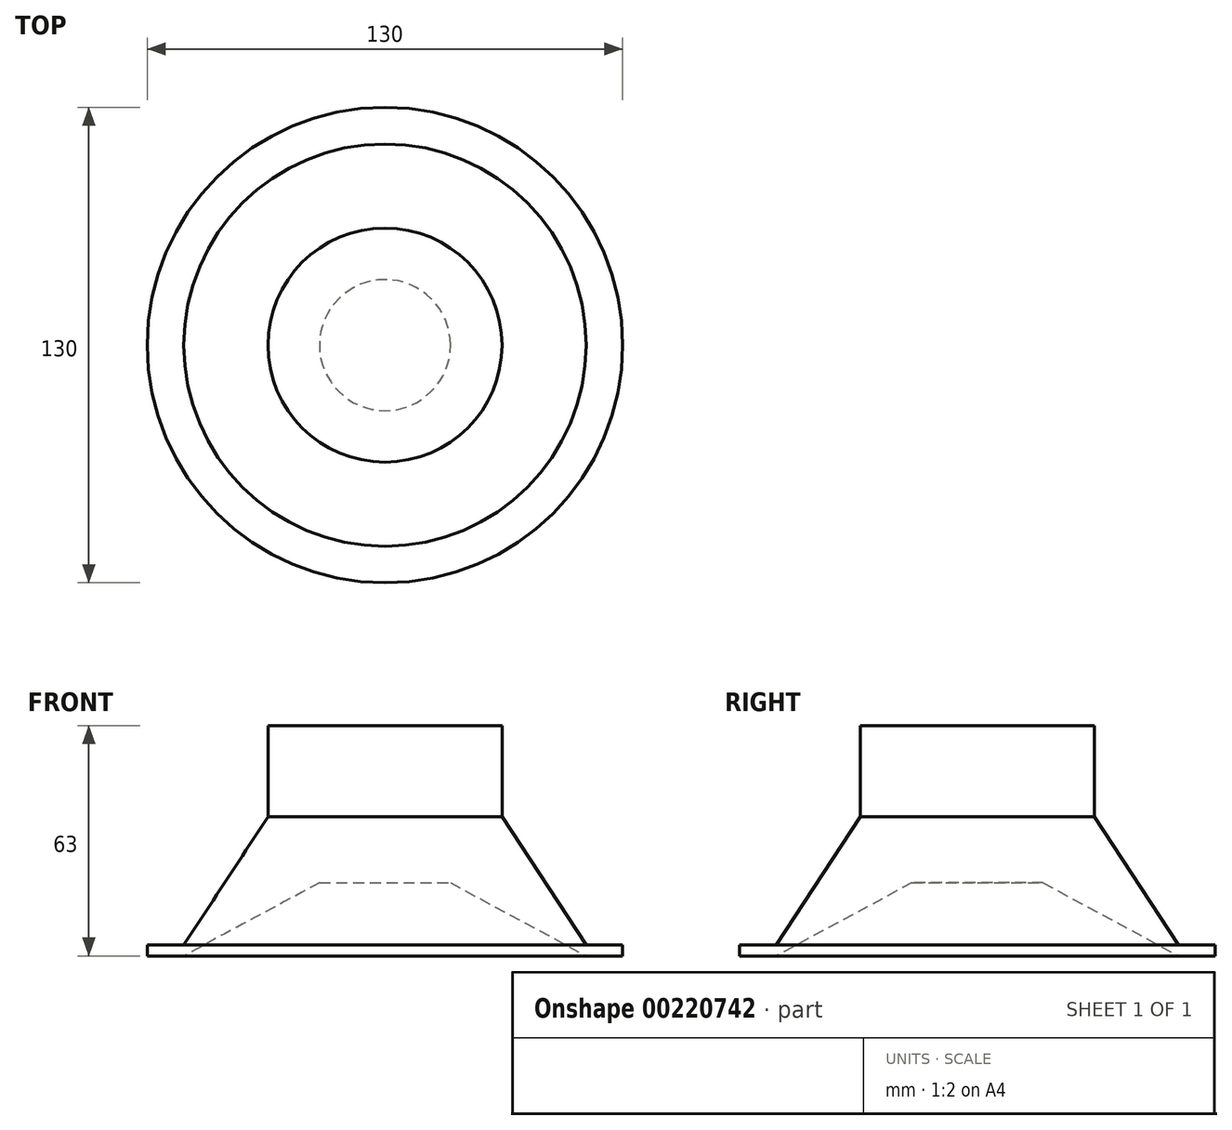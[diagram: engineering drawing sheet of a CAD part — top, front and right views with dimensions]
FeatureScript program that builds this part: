
annotation { "Feature Type Name" : "Feature", "Feature Type Description" : "" }
export const myFeature = defineFeature(function(context is Context, id is Id, definition is map)
    precondition{}
    {
        {
            var Q0;
            Q0=qCreatedBy(makeId("Front.planeOp"),FACE);
            var sketch = newSketch(context, id + "F0", { "sketchPlane" : qUnion([Q0])});
            skLineSegment(sketch, "E0", {"start": v(0, 43) * mm, "end": v(32, 43) * mm});
            skLineSegment(sketch, "E1", {"start": v(32, 43) * mm, "end": v(32, 18) * mm});
            skLineSegment(sketch, "E2", {"start": v(32, 18) * mm, "end": v(55, -17) * mm});
            skLineSegment(sketch, "E3", {"start": v(55, -17) * mm, "end": v(65, -17) * mm});
            skLineSegment(sketch, "E4", {"start": v(65, -17) * mm, "end": v(65, -20) * mm});
            skLineSegment(sketch, "E5", {"start": v(65, -20) * mm, "end": v(55, -20) * mm});
            skLineSegment(sketch, "E6", {"start": v(55, -20) * mm, "end": v(17.91, 0) * mm});
            skLineSegment(sketch, "E7", {"start": v(17.91, 0) * mm, "end": v(0, 0) * mm});
            skLineSegment(sketch, "E8", {"start": v(0, 0) * mm, "end": v(0, 43) * mm});
            skLineSegment(sketch, "E9", {"start": v(0, -54.2) * mm, "end": v(0, 64.6) * mm, "construction": true});
            skSolve(sketch);
        }
        {
            var Q0;
            Q0=makeQuery(id+"F0.imprint","IMPRINT",FACE,{"disambiguationData":[TD([[makeQuery(id+"F0.imprint","IMPRINT",EDGE,{"derivedFrom":sQuery(id+"F0.wireOp",EDGE,"E0")}),-1.0]])]});
            var Q1;
            Q1=sQuery(id+"F0.wireOp",EDGE,"E9");
            var Q2;
            Q2=sQuery(id+"F0.wireOp",EDGE,"E9");
            revolve(context, id + "F1", {"entities" : qUnion([Q0]), "surfaceEntities" : qUnion([Q1]), "axis" : qUnion([Q2]), "revolveType" : RevolveType.FULL});
        }
    });
